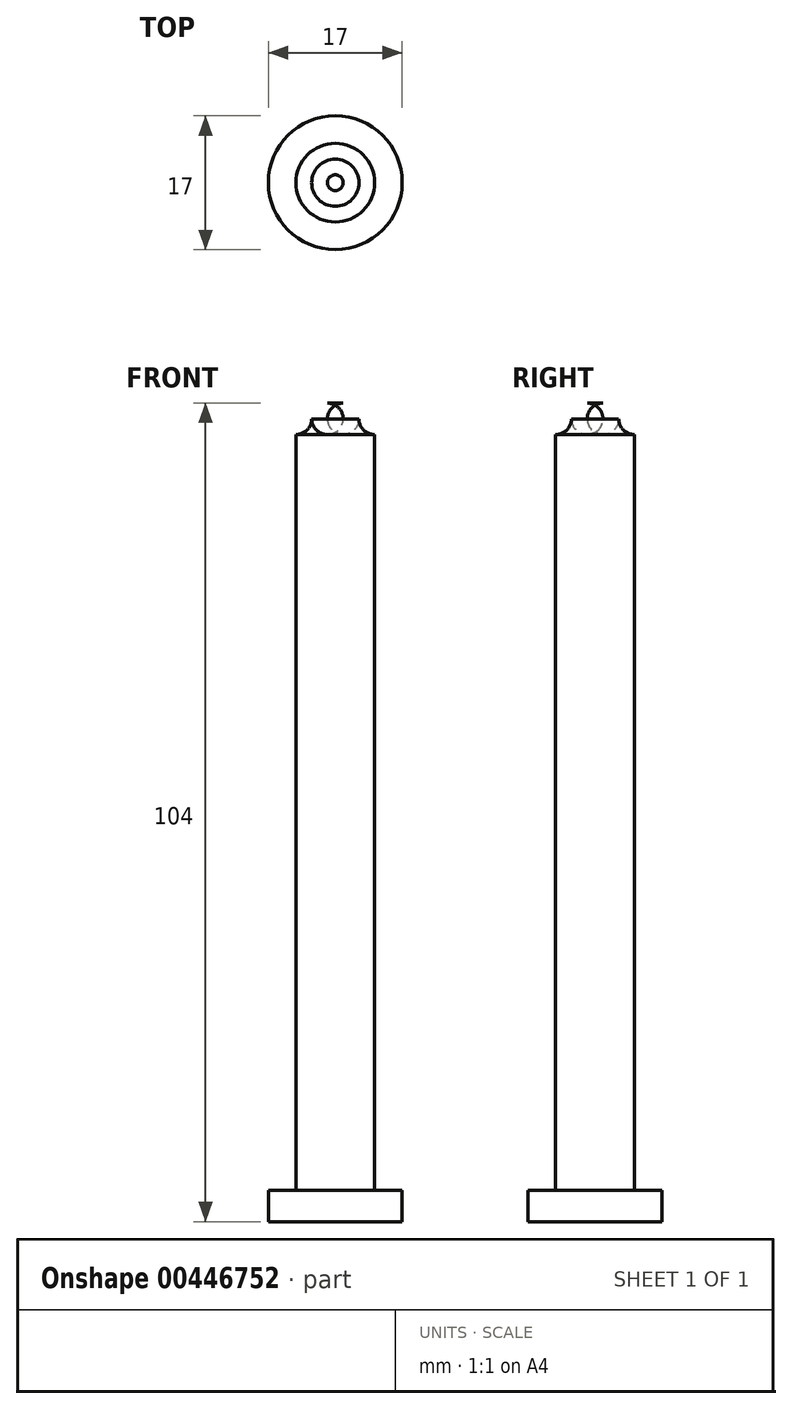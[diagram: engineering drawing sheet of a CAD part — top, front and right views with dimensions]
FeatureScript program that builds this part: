
annotation { "Feature Type Name" : "Feature", "Feature Type Description" : "" }
export const myFeature = defineFeature(function(context is Context, id is Id, definition is map)
    precondition{}
    {
        {
            var Q0;
            Q0=qCreatedBy(makeId("Top.planeOp"),FACE);
            var sketch = newSketch(context, id + "F0", { "sketchPlane" : qUnion([Q0])});
            skCircle(sketch, "E0", {"center": v(0, 0) * mm, "radius": 8.5 * mm});
            skSolve(sketch);
        }
        {
            var Q0;
            Q0=qSketchRegion(id+"F0",true);
            extrude(context, id + "F1", {"entities" : qUnion([Q0]), "depth" : 4 * mm});
        }
        {
            var Q0;
            Q0=qCreatedBy(makeId("Top.planeOp"),FACE);
            var sketch = newSketch(context, id + "F2", { "sketchPlane" : qUnion([Q0])});
            skCircle(sketch, "E1", {"center": v(0, 0) * mm, "radius": 5 * mm});
            skSolve(sketch);
        }
        {
            var Q0;
            Q0=qSketchRegion(id+"F2",true);
            extrude(context, id + "F3", {"entities" : qUnion([Q0]), "operationType" : NewBodyOperationType.ADD, "depth" : 100 * mm});
        }
        {
            var Q0;
            Q0=qCreatedBy(makeId("Right.planeOp"),FACE);
            var sketch = newSketch(context, id + "F4", { "sketchPlane" : qUnion([Q0])});
            skLineSegment(sketch, "E2", {"start": v(0, 102) * mm, "end": v(0, 100) * mm});
            skLineSegment(sketch, "E3", {"start": v(0, 100) * mm, "end": v(5, 100) * mm});
            skLineSegment(sketch, "E4", {"start": v(3, 102) * mm, "end": v(0, 102) * mm});
            skArc(sketch, "E5", {"start": v(3, 102) * mm, "mid": v(3.59, 100.59) * mm, "end": v(5, 100) * mm});
            skSolve(sketch);
        }
        {
            var Q0;
            Q0=makeQuery(id+"F4.imprint","IMPRINT",FACE,{"disambiguationData":[TD([[makeQuery(id+"F4.imprint","IMPRINT",EDGE,{"derivedFrom":sQuery(id+"F4.wireOp",EDGE,"E2")}),1.0]])]});
            var Q1;
            Q1=sQuery(id+"F4.wireOp",EDGE,"E2");
            revolve(context, id + "F5", {"operationType" : NewBodyOperationType.ADD, "entities" : qUnion([Q0]), "axis" : qUnion([Q1]), "revolveType" : RevolveType.FULL});
        }
        {
            var Q0;
            Q0=qCreatedBy(makeId("Right.planeOp"),FACE);
            var sketch = newSketch(context, id + "F6", { "sketchPlane" : qUnion([Q0])});
            skLineSegment(sketch, "E6", {"start": v(0, 102) * mm, "end": v(0, 104) * mm});
            skLineSegment(sketch, "E7", {"start": v(0, 104) * mm, "end": v(1, 104) * mm});
            skLineSegment(sketch, "E8", {"start": v(3, 102) * mm, "end": v(0, 102) * mm});
            skArc(sketch, "E9", {"start": v(3, 102) * mm, "mid": v(2.41, 103.41) * mm, "end": v(1, 104) * mm});
            skSolve(sketch);
        }
        {
            var Q0;
            Q0=makeQuery(id+"F6.imprint","IMPRINT",FACE,{"disambiguationData":[TD([[makeQuery(id+"F6.imprint","IMPRINT",EDGE,{"derivedFrom":sQuery(id+"F6.wireOp",EDGE,"E6")}),-1.0]])]});
            var Q1;
            Q1=sQuery(id+"F6.wireOp",EDGE,"E6");
            revolve(context, id + "F7", {"operationType" : NewBodyOperationType.ADD, "entities" : qUnion([Q0]), "axis" : qUnion([Q1]), "revolveType" : RevolveType.FULL});
        }
    });
